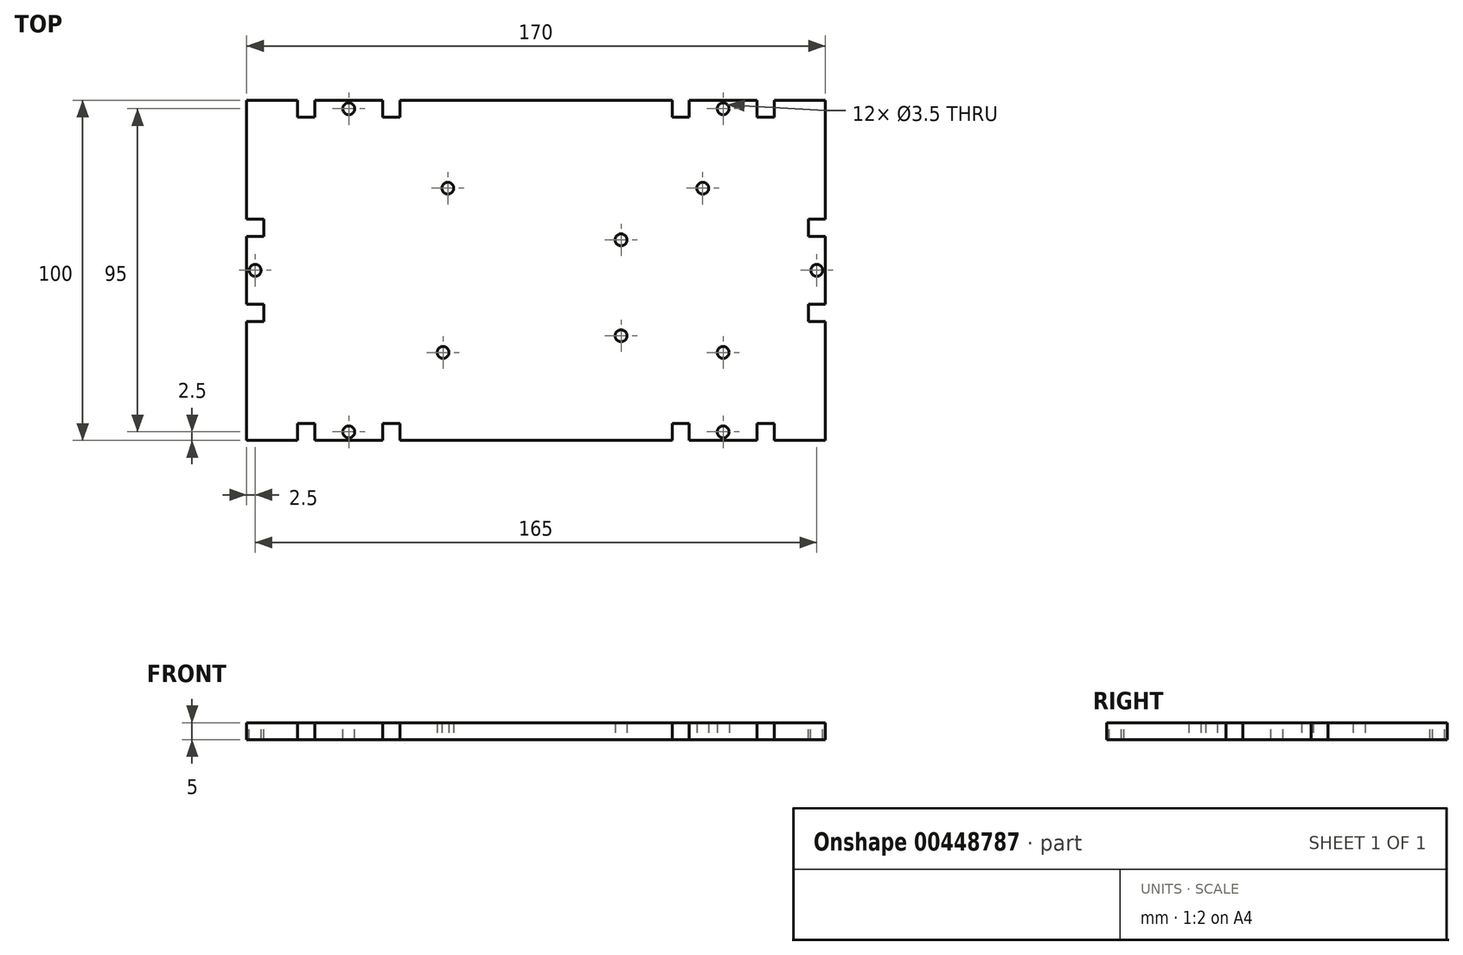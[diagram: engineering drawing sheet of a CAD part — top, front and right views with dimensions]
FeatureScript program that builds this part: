
annotation { "Feature Type Name" : "Feature", "Feature Type Description" : "" }
export const myFeature = defineFeature(function(context is Context, id is Id, definition is map)
    precondition{}
    {
        {
            assignVariable(context, id + "F0", {"name" : "thickness", "anyValue" : 5 * mm});
        }
        {
            var Q0;
            Q0=qCreatedBy(makeId("Top.planeOp"),FACE);
            var sketch = newSketch(context, id + "F1", { "sketchPlane" : qUnion([Q0])});
            skLineSegment(sketch, "E0.bottom", {"start": v(0, 0) * mm, "end": v(101.5, 0) * mm, "construction": true});
            skLineSegment(sketch, "E0.top", {"start": v(0, 53.5) * mm, "end": v(101.5, 53.5) * mm, "construction": true});
            skLineSegment(sketch, "E0.left", {"start": v(0, 0) * mm, "end": v(0, 53.5) * mm, "construction": true});
            skLineSegment(sketch, "E0.right", {"start": v(101.5, 0) * mm, "end": v(101.5, 53.5) * mm, "construction": true});
            skCircle(sketch, "E1", {"center": v(14.2, 2.6) * mm, "radius": 1.75 * mm});
            skCircle(sketch, "E2", {"center": v(15.6, 50.9) * mm, "radius": 1.75 * mm});
            skCircle(sketch, "E3", {"center": v(66.5, 35.7) * mm, "radius": 1.75 * mm});
            skCircle(sketch, "E4", {"center": v(66.5, 7.5) * mm, "radius": 1.75 * mm});
            skCircle(sketch, "E5", {"center": v(90.5, 50.9) * mm, "radius": 1.75 * mm});
            skCircle(sketch, "E6", {"center": v(96.5, 2.6) * mm, "radius": 1.75 * mm});
            skLineSegment(sketch, "E7.bottom", {"start": v(-43.5, 76.75) * mm, "end": v(126.5, 76.75) * mm});
            skLineSegment(sketch, "E7.top", {"start": v(-43.5, -23.25) * mm, "end": v(126.5, -23.25) * mm});
            skLineSegment(sketch, "E7.left", {"start": v(-43.5, 76.75) * mm, "end": v(-43.5, -23.25) * mm});
            skLineSegment(sketch, "E7.right", {"start": v(126.5, 76.75) * mm, "end": v(126.5, -23.25) * mm});
            skPoint(sketch, "E8", {"position": v(-43.5, 26.75) * mm});
            skPoint(sketch, "E9", {"position": v(0, 26.75) * mm});
            skPoint(sketch, "E10", {"position": v(41.5, 76.75) * mm});
            skSolve(sketch);
        }
        {
            var Q0;
            Q0=qSketchRegion(id+"F1",true);
            extrude(context, id + "F2", {"entities" : qUnion([Q0]), "depth" : getVariable(context, 'thickness')});
        }
        {
            var Q0;
            Q0=makeQuery(id+"F2.opExtrude","CAP_FACE",FACE,{"disambiguationData":[OSD([sQuery(id+"F1.wireOp",EDGE,"E1"),sQuery(id+"F1.wireOp",EDGE,"E2"),sQuery(id+"F1.wireOp",EDGE,"E3"),sQuery(id+"F1.wireOp",EDGE,"E4"),sQuery(id+"F1.wireOp",EDGE,"E5"),sQuery(id+"F1.wireOp",EDGE,"E6"),sQuery(id+"F1.wireOp",EDGE,"E7.bottom"),sQuery(id+"F1.wireOp",EDGE,"E7.top"),sQuery(id+"F1.wireOp",EDGE,"E7.left"),sQuery(id+"F1.wireOp",EDGE,"E7.right")])],"isStart":false});
            var sketch = newSketch(context, id + "F3", { "sketchPlane" : qUnion([Q0])});
            skLineSegment(sketch, "E11.0", {"start": v(-38.5, 71.75) * mm, "end": v(-38.5, -18.25) * mm, "construction": true});
            skLineSegment(sketch, "E11.1", {"start": v(-38.5, 71.75) * mm, "end": v(121.5, 71.75) * mm, "construction": true});
            skLineSegment(sketch, "E11.2", {"start": v(121.5, 71.75) * mm, "end": v(121.5, -18.25) * mm, "construction": true});
            skLineSegment(sketch, "E11.3", {"start": v(-38.5, -18.25) * mm, "end": v(121.5, -18.25) * mm, "construction": true});
            skLineSegment(sketch, "E12.bottom", {"start": v(-28.5, -18.25) * mm, "end": v(-23.5, -18.25) * mm});
            skLineSegment(sketch, "E12.top", {"start": v(-28.5, -23.25) * mm, "end": v(-23.5, -23.25) * mm});
            skLineSegment(sketch, "E12.left", {"start": v(-28.5, -18.25) * mm, "end": v(-28.5, -23.25) * mm});
            skLineSegment(sketch, "E12.right", {"start": v(-23.5, -18.25) * mm, "end": v(-23.5, -23.25) * mm});
            skLineSegment(sketch, "E13.bottom", {"start": v(-3.5, -18.25) * mm, "end": v(1.5, -18.25) * mm});
            skLineSegment(sketch, "E13.top", {"start": v(-3.5, -23.25) * mm, "end": v(1.5, -23.25) * mm});
            skLineSegment(sketch, "E13.left", {"start": v(-3.5, -18.25) * mm, "end": v(-3.5, -23.25) * mm});
            skLineSegment(sketch, "E13.right", {"start": v(1.5, -18.25) * mm, "end": v(1.5, -23.25) * mm});
            skCircle(sketch, "E14", {"center": v(-13.5, -20.75) * mm, "radius": 1.75 * mm});
            skLineSegment(sketch, "E15", {"start": v(41.5, -23.25) * mm, "end": v(41.5, 76.75) * mm, "construction": true});
            skLineSegment(sketch, "E16.MirrorCS", {"start": v(81.5, -18.25) * mm, "end": v(81.5, -23.25) * mm});
            skCircle(sketch, "E17.MirrorC", {"center": v(96.5, -20.75) * mm, "radius": 1.75 * mm});
            skLineSegment(sketch, "E18.MirrorCS", {"start": v(86.5, -18.25) * mm, "end": v(86.5, -23.25) * mm});
            skLineSegment(sketch, "E19.MirrorCS", {"start": v(86.5, -23.25) * mm, "end": v(81.5, -23.25) * mm});
            skLineSegment(sketch, "E20.MirrorCS", {"start": v(86.5, -18.25) * mm, "end": v(81.5, -18.25) * mm});
            skLineSegment(sketch, "E21.MirrorCS", {"start": v(106.5, -18.25) * mm, "end": v(106.5, -23.25) * mm});
            skLineSegment(sketch, "E22.MirrorCS", {"start": v(111.5, -18.25) * mm, "end": v(111.5, -23.25) * mm});
            skLineSegment(sketch, "E23.MirrorCS", {"start": v(111.5, -23.25) * mm, "end": v(106.5, -23.25) * mm});
            skLineSegment(sketch, "E24.MirrorCS", {"start": v(111.5, -18.25) * mm, "end": v(106.5, -18.25) * mm});
            skLineSegment(sketch, "E25", {"start": v(-43.5, 26.75) * mm, "end": v(126.5, 26.75) * mm, "construction": true});
            skLineSegment(sketch, "E26.MirrorCS", {"start": v(111.5, 71.75) * mm, "end": v(106.5, 71.75) * mm});
            skLineSegment(sketch, "E27.MirrorCS", {"start": v(86.5, 76.75) * mm, "end": v(81.5, 76.75) * mm});
            skLineSegment(sketch, "E28.MirrorCS", {"start": v(106.5, 71.75) * mm, "end": v(106.5, 76.75) * mm});
            skLineSegment(sketch, "E29.MirrorCS", {"start": v(111.5, 76.75) * mm, "end": v(106.5, 76.75) * mm});
            skLineSegment(sketch, "E30.MirrorCS", {"start": v(111.5, 71.75) * mm, "end": v(111.5, 76.75) * mm});
            skLineSegment(sketch, "E31.MirrorCS", {"start": v(86.5, 71.75) * mm, "end": v(86.5, 76.75) * mm});
            skLineSegment(sketch, "E32.MirrorCS", {"start": v(-28.5, 76.75) * mm, "end": v(-23.5, 76.75) * mm});
            skLineSegment(sketch, "E33.MirrorCS", {"start": v(86.5, 71.75) * mm, "end": v(81.5, 71.75) * mm});
            skCircle(sketch, "E34.MirrorC", {"center": v(-13.5, 74.25) * mm, "radius": 1.75 * mm});
            skLineSegment(sketch, "E35.MirrorCS", {"start": v(-28.5, 71.75) * mm, "end": v(-23.5, 71.75) * mm});
            skLineSegment(sketch, "E36.MirrorCS", {"start": v(1.5, 71.75) * mm, "end": v(1.5, 76.75) * mm});
            skCircle(sketch, "E37.MirrorC", {"center": v(96.5, 74.25) * mm, "radius": 1.75 * mm});
            skLineSegment(sketch, "E38.MirrorCS", {"start": v(-3.5, 71.75) * mm, "end": v(-3.5, 76.75) * mm});
            skLineSegment(sketch, "E39.MirrorCS", {"start": v(-3.5, 76.75) * mm, "end": v(1.5, 76.75) * mm});
            skLineSegment(sketch, "E40.MirrorCS", {"start": v(-23.5, 71.75) * mm, "end": v(-23.5, 76.75) * mm});
            skLineSegment(sketch, "E41.MirrorCS", {"start": v(-28.5, 71.75) * mm, "end": v(-28.5, 76.75) * mm});
            skLineSegment(sketch, "E42.MirrorCS", {"start": v(-3.5, 71.75) * mm, "end": v(1.5, 71.75) * mm});
            skLineSegment(sketch, "E43.MirrorCS", {"start": v(81.5, 71.75) * mm, "end": v(81.5, 76.75) * mm});
            skLineSegment(sketch, "E44.bottom", {"start": v(-38.5, 41.75) * mm, "end": v(-38.5, 36.75) * mm});
            skLineSegment(sketch, "E44.top", {"start": v(-43.5, 41.75) * mm, "end": v(-43.5, 36.75) * mm});
            skLineSegment(sketch, "E44.left", {"start": v(-38.5, 41.75) * mm, "end": v(-43.5, 41.75) * mm});
            skLineSegment(sketch, "E44.right", {"start": v(-38.5, 36.75) * mm, "end": v(-43.5, 36.75) * mm});
            skLineSegment(sketch, "E45.bottom", {"start": v(-38.5, 16.75) * mm, "end": v(-38.5, 11.75) * mm});
            skLineSegment(sketch, "E45.top", {"start": v(-43.5, 16.75) * mm, "end": v(-43.5, 11.75) * mm});
            skLineSegment(sketch, "E45.left", {"start": v(-38.5, 16.75) * mm, "end": v(-43.5, 16.75) * mm});
            skLineSegment(sketch, "E45.right", {"start": v(-38.5, 11.75) * mm, "end": v(-43.5, 11.75) * mm});
            skCircle(sketch, "E46", {"center": v(-41, 26.75) * mm, "radius": 1.75 * mm});
            skLineSegment(sketch, "E47.MirrorCS", {"start": v(121.5, 36.75) * mm, "end": v(126.5, 36.75) * mm});
            skLineSegment(sketch, "E48.MirrorCS", {"start": v(121.5, 11.75) * mm, "end": v(126.5, 11.75) * mm});
            skLineSegment(sketch, "E49.MirrorCS", {"start": v(121.5, 41.75) * mm, "end": v(126.5, 41.75) * mm});
            skLineSegment(sketch, "E50.MirrorCS", {"start": v(126.5, 16.75) * mm, "end": v(126.5, 11.75) * mm});
            skLineSegment(sketch, "E51.MirrorCS", {"start": v(126.5, 41.75) * mm, "end": v(126.5, 36.75) * mm});
            skLineSegment(sketch, "E52.MirrorCS", {"start": v(121.5, 16.75) * mm, "end": v(126.5, 16.75) * mm});
            skLineSegment(sketch, "E53.MirrorCS", {"start": v(121.5, 41.75) * mm, "end": v(121.5, 36.75) * mm});
            skCircle(sketch, "E54.MirrorC", {"center": v(124, 26.75) * mm, "radius": 1.75 * mm});
            skLineSegment(sketch, "E55.MirrorCS", {"start": v(121.5, 16.75) * mm, "end": v(121.5, 11.75) * mm});
            skSolve(sketch);
        }
        {
            var Q0;
            Q0=qSketchRegion(id+"F3",true);
            var Q1;
            Q1=makeQuery(id+"F2.opExtrude","CAP_FACE",FACE,{"disambiguationData":[OSD([sQuery(id+"F1.wireOp",EDGE,"E1"),sQuery(id+"F1.wireOp",EDGE,"E2"),sQuery(id+"F1.wireOp",EDGE,"E3"),sQuery(id+"F1.wireOp",EDGE,"E4"),sQuery(id+"F1.wireOp",EDGE,"E5"),sQuery(id+"F1.wireOp",EDGE,"E6"),sQuery(id+"F1.wireOp",EDGE,"E7.bottom"),sQuery(id+"F1.wireOp",EDGE,"E7.top"),sQuery(id+"F1.wireOp",EDGE,"E7.left"),sQuery(id+"F1.wireOp",EDGE,"E7.right")])],"isStart":true});
            extrude(context, id + "F4", {"entities" : qUnion([Q0]), "operationType" : NewBodyOperationType.REMOVE, "endBound" : BoundingType.UP_TO_SURFACE, "oppositeDirection" : true, "endBoundEntityFace" : qUnion([Q1]), "depth" : 25 * mm});
        }
    });
